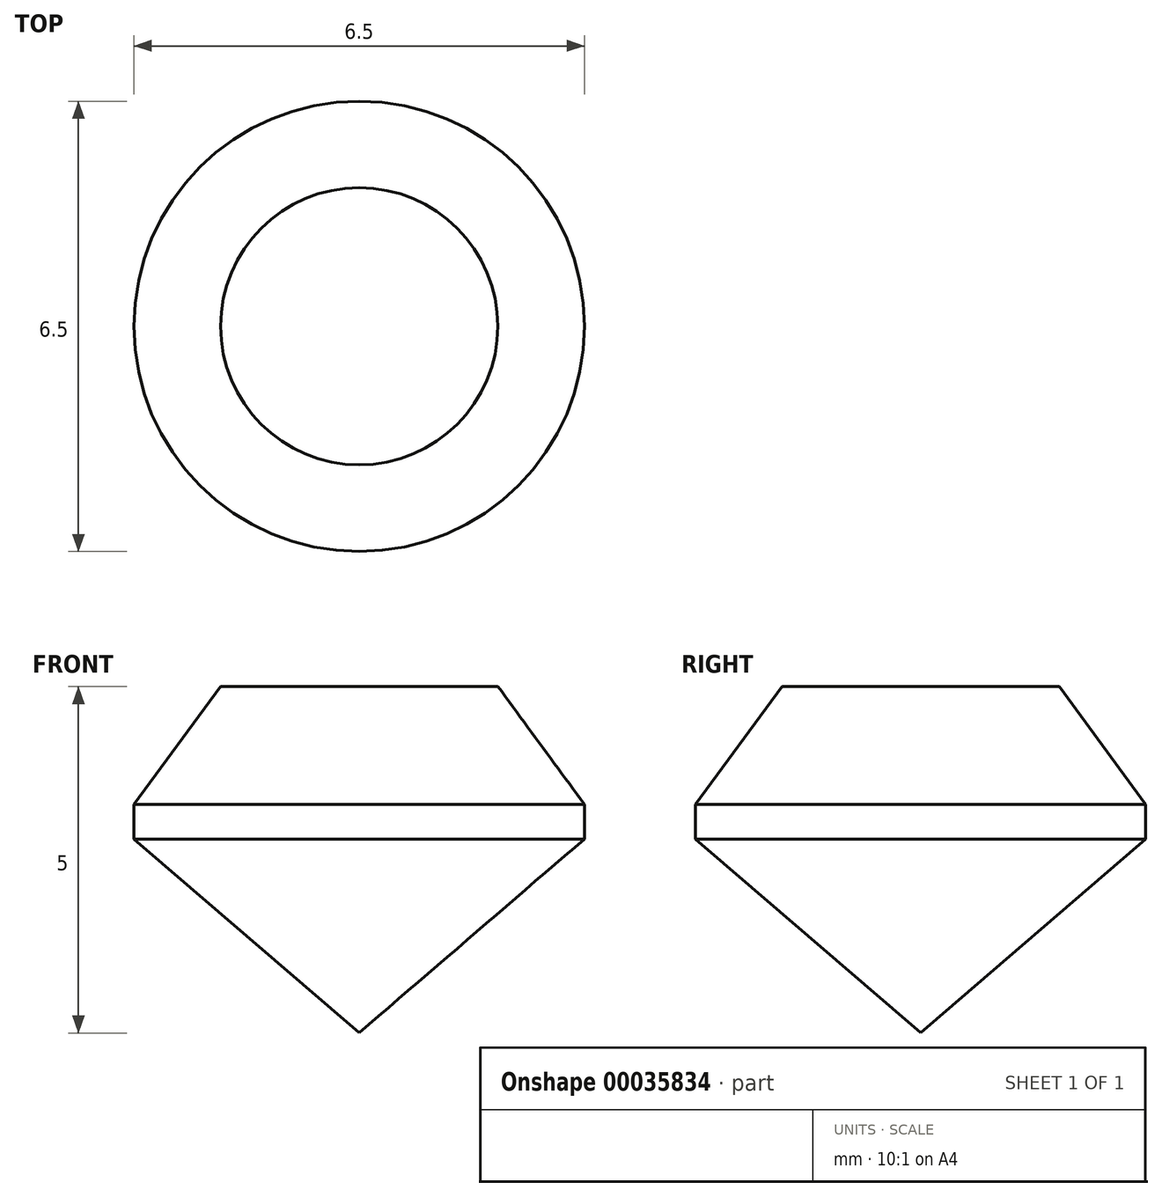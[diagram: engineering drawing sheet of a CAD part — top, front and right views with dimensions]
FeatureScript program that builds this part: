
annotation { "Feature Type Name" : "Feature", "Feature Type Description" : "" }
export const myFeature = defineFeature(function(context is Context, id is Id, definition is map)
    precondition{}
    {
        {
            var Q0;
            Q0=qCreatedBy(makeId("Front.planeOp"),FACE);
            var sketch = newSketch(context, id + "F0", { "sketchPlane" : qUnion([Q0])});
            skLineSegment(sketch, "E0", {"start": v(0, 2.2) * mm, "end": v(2, 2.2) * mm});
            skLineSegment(sketch, "E1", {"start": v(2, 2.2) * mm, "end": v(3.25, 0.5) * mm});
            skLineSegment(sketch, "E2", {"start": v(3.25, 0.5) * mm, "end": v(3.25, 0) * mm});
            skLineSegment(sketch, "E3", {"start": v(3.25, 0) * mm, "end": v(0, -2.8) * mm});
            skLineSegment(sketch, "E4", {"start": v(0, -2.8) * mm, "end": v(0, 2.2) * mm});
            skSolve(sketch);
        }
        {
            var Q0;
            Q0=qCreatedBy(makeId("Front.planeOp"),FACE);
            var sketch = newSketch(context, id + "F1", { "sketchPlane" : qUnion([Q0])});
            skLineSegment(sketch, "E5", {"start": v(0, 4.63) * mm, "end": v(0, -4.7) * mm});
            skSolve(sketch);
        }
        {
            var Q0;
            Q0 = qSketchRegion(id + "F0", true);
            var Q1;
            Q1=sQuery(id+"F1.wireOp",EDGE,"E5");
            revolve(context, id + "F2", {"entities" : qUnion([Q0]), "axis" : qUnion([Q1]), "revolveType" : RevolveType.FULL});
        }
    });
